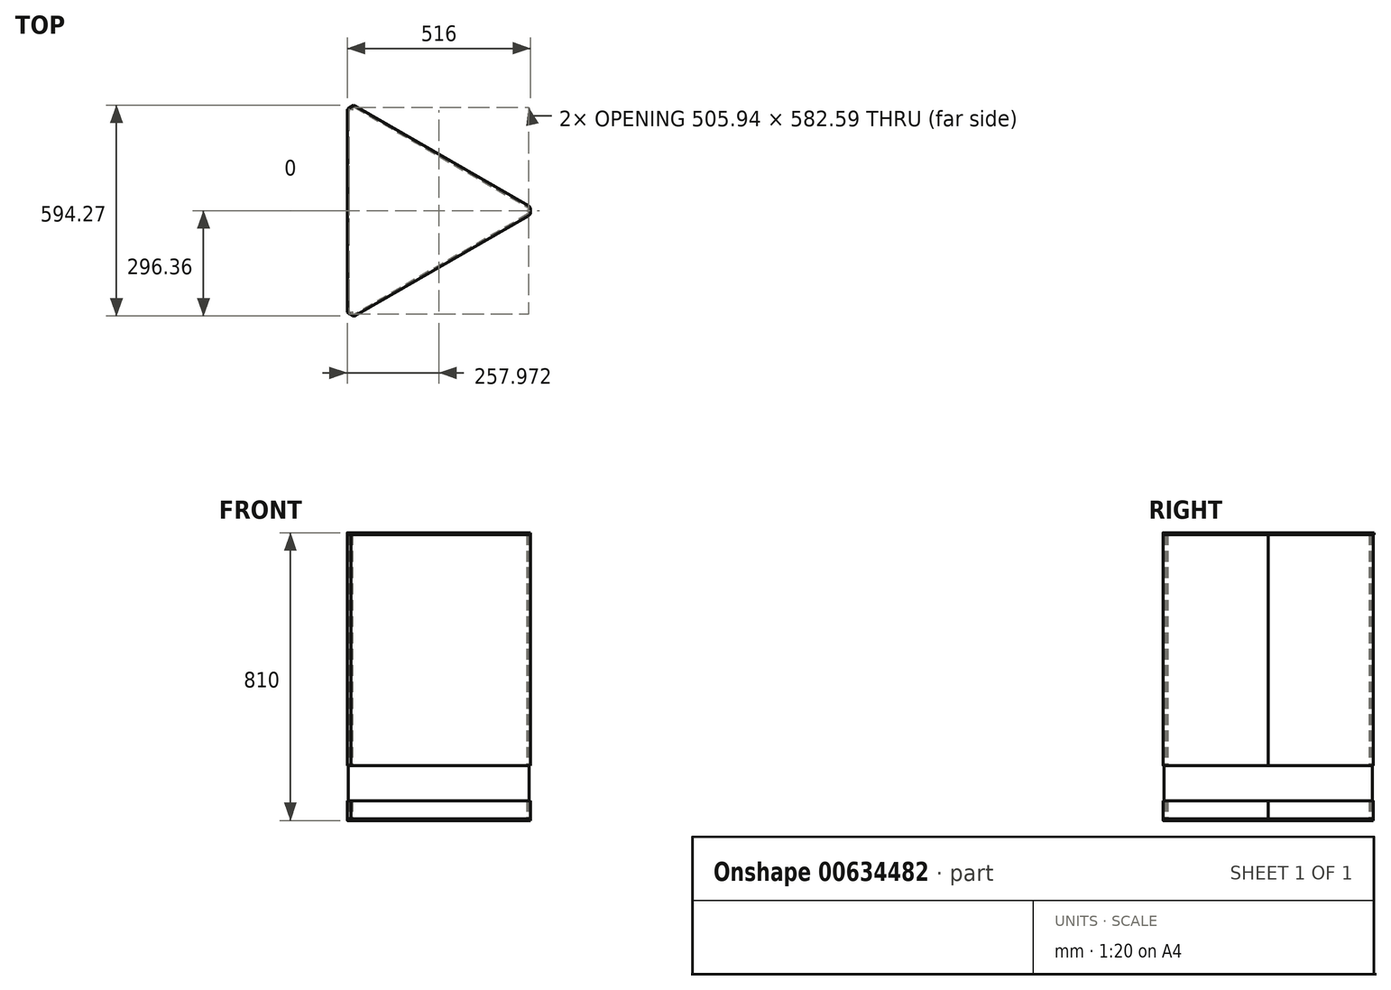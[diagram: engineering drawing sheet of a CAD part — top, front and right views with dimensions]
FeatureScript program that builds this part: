
annotation { "Feature Type Name" : "Feature", "Feature Type Description" : "" }
export const myFeature = defineFeature(function(context is Context, id is Id, definition is map)
    precondition{}
    {
        {
            var Q0;
            Q0=qCreatedBy(makeId("Top.planeOp"),FACE);
            var sketch = newSketch(context, id + "F0", { "sketchPlane" : qUnion([Q0])});
            skLineSegment(sketch, "E0", {"start": v(16.16, 290.67) * mm, "end": v(503.45, 9.33) * mm});
            skLineSegment(sketch, "E1", {"start": v(503.45, -9.33) * mm, "end": v(16.16, -290.67) * mm});
            skPoint(sketch, "E2.visualSharp", {"position": v(0, 300) * mm});
            skArc(sketch, "E2.filletArc", {"start": v(16.16, 290.67) * mm, "mid": v(10.12, 289.88) * mm, "end": v(9.33, 283.84) * mm});
            skLineSegment(sketch, "E3", {"start": v(0, -281.34) * mm, "end": v(0, 281.34) * mm});
            skArc(sketch, "E4.filletArc", {"start": v(9.33, 283.84) * mm, "mid": v(3.7, 286.17) * mm, "end": v(0, 281.34) * mm});
            skPoint(sketch, "E5.visualSharp", {"position": v(519.62, 0) * mm});
            skArc(sketch, "E5.filletArc", {"start": v(500.95, 0) * mm, "mid": v(505.78, 3.7) * mm, "end": v(503.45, 9.33) * mm});
            skPoint(sketch, "E6.visualSharp", {"position": v(0, -300) * mm});
            skArc(sketch, "E6.filletArc", {"start": v(0, -281.34) * mm, "mid": v(3.7, -286.17) * mm, "end": v(9.33, -283.84) * mm});
            skArc(sketch, "E7.filletArc", {"start": v(9.33, -283.84) * mm, "mid": v(10.12, -289.88) * mm, "end": v(16.16, -290.67) * mm});
            skArc(sketch, "E8.filletArc", {"start": v(503.45, -9.33) * mm, "mid": v(505.78, -3.7) * mm, "end": v(500.95, 0) * mm});
            skSolve(sketch);
        }
        {
            var Q0;
            Q0=qSketchRegion(id+"F0",true);
            extrude(context, id + "F1", {"entities" : qUnion([Q0]), "depth" : 800 * mm, "offsetDistance" : 25 * mm});
        }
        {
            var Q0;
            Q0=makeQuery(id+"F1.opExtrude","CAP_FACE",FACE,{"disambiguationData":[OSD([sQuery(id+"F0.wireOp",EDGE,"E0"),sQuery(id+"F0.wireOp",EDGE,"E1"),sQuery(id+"F0.wireOp",EDGE,"E2.filletArc"),sQuery(id+"F0.wireOp",EDGE,"E3"),sQuery(id+"F0.wireOp",EDGE,"E4.filletArc"),sQuery(id+"F0.wireOp",EDGE,"E5.filletArc"),sQuery(id+"F0.wireOp",EDGE,"E6.filletArc"),sQuery(id+"F0.wireOp",EDGE,"E7.filletArc"),sQuery(id+"F0.wireOp",EDGE,"E8.filletArc")])],"isStart":false});
            var Q1;
            Q1=makeQuery(id+"F1.opExtrude","CAP_FACE",FACE,{"disambiguationData":[OSD([sQuery(id+"F0.wireOp",EDGE,"E0"),sQuery(id+"F0.wireOp",EDGE,"E1"),sQuery(id+"F0.wireOp",EDGE,"E2.filletArc"),sQuery(id+"F0.wireOp",EDGE,"E3"),sQuery(id+"F0.wireOp",EDGE,"E4.filletArc"),sQuery(id+"F0.wireOp",EDGE,"E5.filletArc"),sQuery(id+"F0.wireOp",EDGE,"E6.filletArc"),sQuery(id+"F0.wireOp",EDGE,"E7.filletArc"),sQuery(id+"F0.wireOp",EDGE,"E8.filletArc")])],"isStart":true});
            var Q2;
            Q2=makeQuery(id+"F1.opExtrude","SWEPT_BODY",BODY,{"disambiguationData":[OSD([sQuery(id+"F0.wireOp",EDGE,"E0"),sQuery(id+"F0.wireOp",EDGE,"E1"),sQuery(id+"F0.wireOp",EDGE,"E2.filletArc"),sQuery(id+"F0.wireOp",EDGE,"E3"),sQuery(id+"F0.wireOp",EDGE,"E4.filletArc"),sQuery(id+"F0.wireOp",EDGE,"E5.filletArc"),sQuery(id+"F0.wireOp",EDGE,"E6.filletArc"),sQuery(id+"F0.wireOp",EDGE,"E7.filletArc"),sQuery(id+"F0.wireOp",EDGE,"E8.filletArc")])]});
            shell(context, id + "F2", {"entities" : qUnion([Q0, Q1]), "parts" : qUnion([Q2]), "thickness" : 5 * mm, "oppositeDirection" : true});
        }
        {
            var Q0;
            Q0=makeQuery(id+"F1.opExtrude","SWEPT_FACE",FACE,{"disambiguationData":[OSD([sQuery(id+"F0.wireOp",EDGE,"E1")])]});
            var sketch = newSketch(context, id + "F3", { "sketchPlane" : qUnion([Q0])});
            skLineSegment(sketch, "E9.bottom", {"start": v(-242.56, 150) * mm, "end": v(507.44, 150) * mm});
            skLineSegment(sketch, "E9.top", {"start": v(-242.56, 50) * mm, "end": v(507.44, 50) * mm});
            skLineSegment(sketch, "E9.left", {"start": v(-242.56, 150) * mm, "end": v(-242.56, 50) * mm});
            skLineSegment(sketch, "E9.right", {"start": v(507.44, 150) * mm, "end": v(507.44, 50) * mm});
            skSolve(sketch);
        }
        {
            var Q0;
            Q0=qSketchRegion(id+"F3",true);
            extrude(context, id + "F4", {"entities" : qUnion([Q0]), "operationType" : NewBodyOperationType.REMOVE, "endBound" : BoundingType.THROUGH_ALL, "oppositeDirection" : true, "depth" : 25 * mm, "offsetDistance" : 25 * mm});
        }
        {
            var Q0;
            Q0=makeQuery(id+"F4.boolean.opBoolean","COPY",FACE,{"derivedFrom":makeQuery(id+"F4.opExtrude","SWEPT_FACE",FACE,{"disambiguationData":[OSD([sQuery(id+"F3.wireOp",EDGE,"E9.top")])]})});
            var sketch = newSketch(context, id + "F5", { "sketchPlane" : qUnion([Q0])});
            skLineSegment(sketch, "E10.0", {"start": v(14.39, 294.58) * mm, "end": v(507.73, 9.75) * mm});
            skLineSegment(sketch, "E11.0", {"start": v(507.73, -9.75) * mm, "end": v(14.39, -294.58) * mm});
            skLineSegment(sketch, "E12.0", {"start": v(-2.5, -284.83) * mm, "end": v(-2.5, 284.83) * mm});
            skLineSegment(sketch, "E13", {"start": v(507.73, 9.75) * mm, "end": v(507.73, -9.75) * mm});
            skLineSegment(sketch, "E14", {"start": v(14.39, -294.58) * mm, "end": v(-2.5, -284.83) * mm});
            skLineSegment(sketch, "E15", {"start": v(-2.5, 284.83) * mm, "end": v(14.39, 294.58) * mm});
            skSolve(sketch);
        }
        {
            var Q0;
            Q0=qSketchRegion(id+"F5",true);
            extrude(context, id + "F6", {"entities" : qUnion([Q0]), "depth" : 100 * mm, "offsetDistance" : 25 * mm});
        }
        {
            var Q0;
            Q0=makeQuery(id+"F6.opExtrude","SWEPT_EDGE",EDGE,{"disambiguationData":[OSD([sQuery(id+"F5.wireOp",EDGE,"E12.0"),sQuery(id+"F5.wireOp",EDGE,"E15")])]});
            var Q1;
            Q1=makeQuery(id+"F6.opExtrude","SWEPT_EDGE",EDGE,{"disambiguationData":[OSD([sQuery(id+"F5.wireOp",EDGE,"E10.0"),sQuery(id+"F5.wireOp",EDGE,"E15")])]});
            var Q2;
            Q2=makeQuery(id+"F6.opExtrude","SWEPT_EDGE",EDGE,{"disambiguationData":[OSD([sQuery(id+"F5.wireOp",EDGE,"E12.0"),sQuery(id+"F5.wireOp",EDGE,"E14")])]});
            var Q3;
            Q3=makeQuery(id+"F6.opExtrude","SWEPT_EDGE",EDGE,{"disambiguationData":[OSD([sQuery(id+"F5.wireOp",EDGE,"E11.0"),sQuery(id+"F5.wireOp",EDGE,"E14")])]});
            var Q4;
            Q4=makeQuery(id+"F6.opExtrude","SWEPT_EDGE",EDGE,{"disambiguationData":[OSD([sQuery(id+"F5.wireOp",EDGE,"E11.0"),sQuery(id+"F5.wireOp",EDGE,"E13")])]});
            var Q5;
            Q5=makeQuery(id+"F6.opExtrude","SWEPT_EDGE",EDGE,{"disambiguationData":[OSD([sQuery(id+"F5.wireOp",EDGE,"E10.0"),sQuery(id+"F5.wireOp",EDGE,"E13")])]});
            fillet(context, id + "F7", {"entities" : qUnion([Q0, Q1, Q2, Q3, Q4, Q5]), "radius" : 5 * mm, "tangentPropagation" : true, "allowEdgeOverflow" : false});
        }
        {
            var Q0;
            Q0=makeQuery(id+"F1.opExtrude","CAP_FACE",FACE,{"disambiguationData":[OSD([sQuery(id+"F0.wireOp",EDGE,"E0"),sQuery(id+"F0.wireOp",EDGE,"E1"),sQuery(id+"F0.wireOp",EDGE,"E2.filletArc"),sQuery(id+"F0.wireOp",EDGE,"E3"),sQuery(id+"F0.wireOp",EDGE,"E4.filletArc"),sQuery(id+"F0.wireOp",EDGE,"E5.filletArc"),sQuery(id+"F0.wireOp",EDGE,"E6.filletArc"),sQuery(id+"F0.wireOp",EDGE,"E7.filletArc"),sQuery(id+"F0.wireOp",EDGE,"E8.filletArc")])],"isStart":false});
            var sketch = newSketch(context, id + "F8", { "sketchPlane" : qUnion([Q0])});
            skLineSegment(sketch, "E16.0", {"start": v(18.66, 295) * mm, "end": v(505.95, 13.66) * mm});
            skLineSegment(sketch, "E16.1", {"start": v(-5, -281.34) * mm, "end": v(-5, 281.34) * mm});
            skLineSegment(sketch, "E16.2", {"start": v(505.95, -13.66) * mm, "end": v(18.66, -295) * mm});
            skPoint(sketch, "E17.endSnap0", {"position": v(11.07, 296) * mm});
            skPoint(sketch, "E18.0", {"position": v(-2.07, 288.41) * mm});
            skLineSegment(sketch, "E19", {"start": v(18.66, 295) * mm, "end": v(13.62, 297.91) * mm});
            skLineSegment(sketch, "E20", {"start": v(-5, 281.34) * mm, "end": v(-5, 287.16) * mm});
            skPoint(sketch, "E21.startSnap0", {"position": v(10.12, 289.88) * mm});
            skPoint(sketch, "E21.endSnap0", {"position": v(10.12, 289.88) * mm});
            skLineSegment(sketch, "E22", {"start": v(-5, 287.16) * mm, "end": v(13.62, 297.91) * mm});
            skPoint(sketch, "E23.orphan", {"position": v(8.58, 300.82) * mm});
            skLineSegment(sketch, "E24", {"start": v(0, 0) * mm, "end": v(79.22, 0) * mm, "construction": true});
            skLineSegment(sketch, "E25.MirrorCS", {"start": v(-5, -281.34) * mm, "end": v(-5, -287.16) * mm});
            skLineSegment(sketch, "E26.MirrorCS", {"start": v(-5, -287.16) * mm, "end": v(13.62, -297.91) * mm});
            skLineSegment(sketch, "E27.MirrorCS", {"start": v(18.66, -295) * mm, "end": v(13.62, -297.91) * mm});
            skPoint(sketch, "E28.MirrorP", {"position": v(11.07, -296) * mm});
            skPoint(sketch, "E29.MirrorP", {"position": v(10.12, -289.88) * mm});
            skPoint(sketch, "E30.MirrorP", {"position": v(8.58, -300.82) * mm});
            skPoint(sketch, "E31.MirrorP", {"position": v(-2.07, -288.41) * mm});
            skLineSegment(sketch, "E32", {"start": v(505.95, 13.66) * mm, "end": v(511, 10.75) * mm});
            skLineSegment(sketch, "E33", {"start": v(505.95, -13.66) * mm, "end": v(511, -10.75) * mm});
            skLineSegment(sketch, "E34", {"start": v(511, 10.75) * mm, "end": v(511, -10.75) * mm});
            skSolve(sketch);
        }
        {
            var Q0;
            Q0=qSketchRegion(id+"F8",true);
            extrude(context, id + "F9", {"entities" : qUnion([Q0]), "depth" : 5 * mm, "offsetDistance" : 25 * mm});
        }
        {
            var Q0;
            Q0=makeQuery(id+"F1.opExtrude","CAP_FACE",FACE,{"disambiguationData":[OSD([sQuery(id+"F0.wireOp",EDGE,"E0"),sQuery(id+"F0.wireOp",EDGE,"E1"),sQuery(id+"F0.wireOp",EDGE,"E2.filletArc"),sQuery(id+"F0.wireOp",EDGE,"E3"),sQuery(id+"F0.wireOp",EDGE,"E4.filletArc"),sQuery(id+"F0.wireOp",EDGE,"E5.filletArc"),sQuery(id+"F0.wireOp",EDGE,"E6.filletArc"),sQuery(id+"F0.wireOp",EDGE,"E7.filletArc"),sQuery(id+"F0.wireOp",EDGE,"E8.filletArc")])],"isStart":true});
            var sketch = newSketch(context, id + "F10", { "sketchPlane" : qUnion([Q0])});
            skLineSegment(sketch, "E35.0.0", {"start": v(-5, -287.16) * mm, "end": v(-5, 287.16) * mm});
            skLineSegment(sketch, "E35.0.1", {"start": v(-5, 287.16) * mm, "end": v(13.62, 297.91) * mm});
            skLineSegment(sketch, "E35.0.2", {"start": v(13.62, 297.91) * mm, "end": v(511, 10.75) * mm});
            skLineSegment(sketch, "E35.0.3", {"start": v(511, 10.75) * mm, "end": v(511, -10.75) * mm});
            skLineSegment(sketch, "E35.0.4", {"start": v(511, -10.75) * mm, "end": v(13.62, -297.91) * mm});
            skLineSegment(sketch, "E35.0.5", {"start": v(13.62, -297.91) * mm, "end": v(-5, -287.16) * mm});
            skSolve(sketch);
        }
        {
            var Q0;
            Q0=qSketchRegion(id+"F10",true);
            extrude(context, id + "F11", {"entities" : qUnion([Q0]), "depth" : 5 * mm, "offsetDistance" : 25 * mm});
        }
        {
            var Q0;
            Q0=makeQuery(id+"F9.opExtrude","SWEPT_EDGE",EDGE,{"disambiguationData":[OSD([sQuery(id+"F8.wireOp",EDGE,"E20"),sQuery(id+"F8.wireOp",EDGE,"E22")])]});
            var Q1;
            Q1=makeQuery(id+"F11.opExtrude","SWEPT_EDGE",EDGE,{"disambiguationData":[OSD([sQuery(id+"F10.wireOp",EDGE,"E35.0.0"),sQuery(id+"F10.wireOp",EDGE,"E35.0.5")])]});
            var Q2;
            Q2=makeQuery(id+"F11.opExtrude","SWEPT_EDGE",EDGE,{"disambiguationData":[OSD([sQuery(id+"F10.wireOp",EDGE,"E35.0.4"),sQuery(id+"F10.wireOp",EDGE,"E35.0.5")])]});
            var Q3;
            Q3=makeQuery(id+"F11.opExtrude","SWEPT_EDGE",EDGE,{"disambiguationData":[OSD([sQuery(id+"F10.wireOp",EDGE,"E35.0.0"),sQuery(id+"F10.wireOp",EDGE,"E35.0.1")])]});
            var Q4;
            Q4=makeQuery(id+"F11.opExtrude","SWEPT_EDGE",EDGE,{"disambiguationData":[OSD([sQuery(id+"F10.wireOp",EDGE,"E35.0.1"),sQuery(id+"F10.wireOp",EDGE,"E35.0.2")])]});
            var Q5;
            Q5=makeQuery(id+"F11.opExtrude","SWEPT_EDGE",EDGE,{"disambiguationData":[OSD([sQuery(id+"F10.wireOp",EDGE,"E35.0.3"),sQuery(id+"F10.wireOp",EDGE,"E35.0.4")])]});
            var Q6;
            Q6=makeQuery(id+"F11.opExtrude","SWEPT_EDGE",EDGE,{"disambiguationData":[OSD([sQuery(id+"F10.wireOp",EDGE,"E35.0.2"),sQuery(id+"F10.wireOp",EDGE,"E35.0.3")])]});
            var Q7;
            Q7=makeQuery(id+"F9.opExtrude","SWEPT_EDGE",EDGE,{"disambiguationData":[OSD([sQuery(id+"F8.wireOp",EDGE,"E32"),sQuery(id+"F8.wireOp",EDGE,"E34")])]});
            var Q8;
            Q8=makeQuery(id+"F9.opExtrude","SWEPT_EDGE",EDGE,{"disambiguationData":[OSD([sQuery(id+"F8.wireOp",EDGE,"E33"),sQuery(id+"F8.wireOp",EDGE,"E34")])]});
            var Q9;
            Q9=makeQuery(id+"F9.opExtrude","SWEPT_EDGE",EDGE,{"disambiguationData":[OSD([sQuery(id+"F8.wireOp",EDGE,"E26.MirrorCS"),sQuery(id+"F8.wireOp",EDGE,"E27.MirrorCS")])]});
            var Q10;
            Q10=makeQuery(id+"F9.opExtrude","SWEPT_EDGE",EDGE,{"disambiguationData":[OSD([sQuery(id+"F8.wireOp",EDGE,"E25.MirrorCS"),sQuery(id+"F8.wireOp",EDGE,"E26.MirrorCS")])]});
            fillet(context, id + "F12", {"entities" : qUnion([Q0, Q1, Q2, Q3, Q4, Q5, Q6, Q7, Q8, Q9, Q10]), "radius" : 10 * mm, "tangentPropagation" : true, "allowEdgeOverflow" : false});
        }
    });
